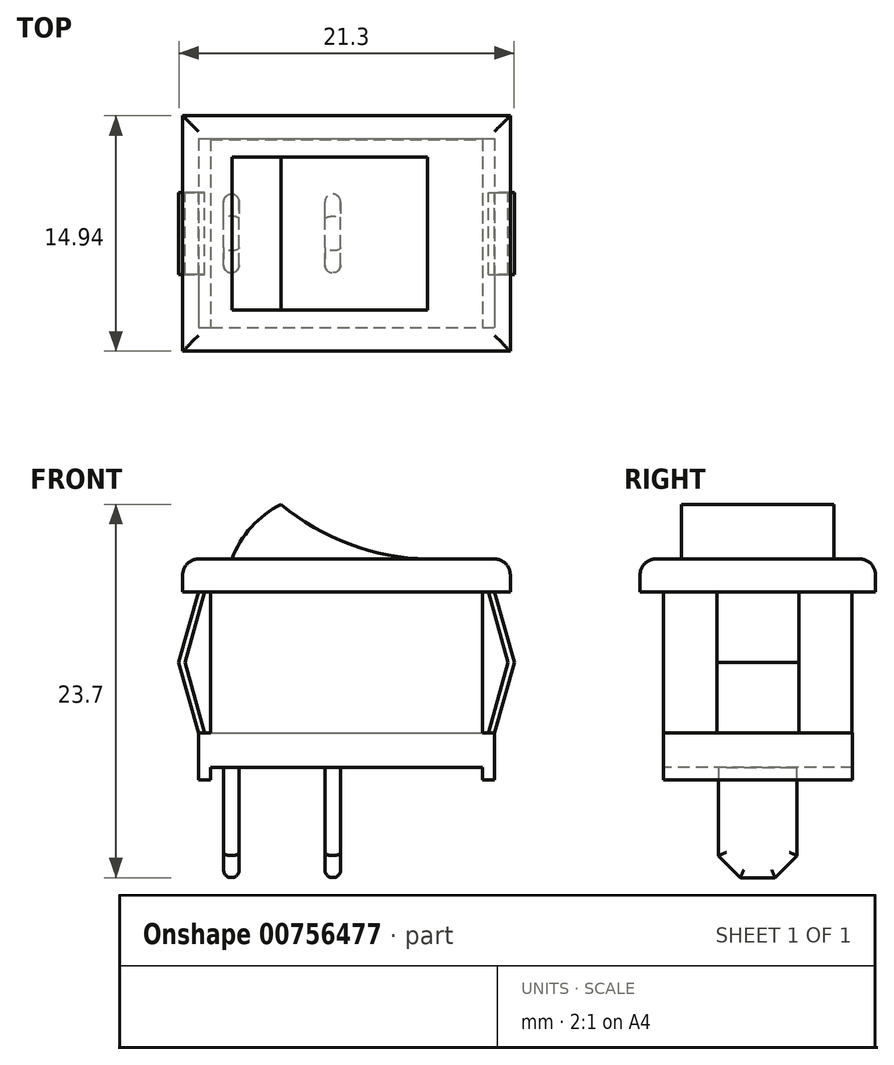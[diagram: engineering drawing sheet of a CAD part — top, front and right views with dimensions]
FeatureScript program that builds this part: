
annotation { "Feature Type Name" : "Feature", "Feature Type Description" : "" }
export const myFeature = defineFeature(function(context is Context, id is Id, definition is map)
    precondition{}
    {
        {
            var Q0;
            Q0=qCreatedBy(makeId("Front.planeOp"),FACE);
            var sketch = newSketch(context, id + "F0", { "sketchPlane" : qUnion([Q0])});
            skLineSegment(sketch, "E0.bottom", {"start": v(-8.62, -5.47) * mm, "end": v(8.62, -5.47) * mm});
            skLineSegment(sketch, "E0.top", {"start": v(-8.62, 5.47) * mm, "end": v(8.62, 5.47) * mm});
            skLineSegment(sketch, "E0.left", {"start": v(-8.62, -5.48) * mm, "end": v(-8.62, 5.47) * mm});
            skLineSegment(sketch, "E0.right", {"start": v(8.62, -5.48) * mm, "end": v(8.62, 5.47) * mm});
            skPoint(sketch, "E0.middle", {"position": v(0, 0) * mm});
            skSolve(sketch);
        }
        {
            var Q0;
            Q0=makeQuery(id+"F0.imprint","IMPRINT",FACE,{"disambiguationData":[TD([[makeQuery(id+"F0.imprint","IMPRINT",EDGE,{"derivedFrom":sQuery(id+"F0.wireOp",EDGE,"E0.bottom")}),1.0]])]});
            extrude(context, id + "F1", {"entities" : qUnion([Q0]), "depth" : 11.95 * mm, "offsetDistance" : 25 * mm, "symmetric" : true});
        }
        {
            var Q0;
            Q0=makeQuery(id+"F1.opExtrude","CAP_FACE",FACE,{"disambiguationData":[OSD([sQuery(id+"F0.wireOp",EDGE,"E0.bottom"),sQuery(id+"F0.wireOp",EDGE,"E0.top"),sQuery(id+"F0.wireOp",EDGE,"E0.left"),sQuery(id+"F0.wireOp",EDGE,"E0.right")])],"isStart":false});
            var sketch = newSketch(context, id + "F2", { "sketchPlane" : qUnion([Q0])});
            skLineSegment(sketch, "E1.0", {"start": v(8.62, -5.48) * mm, "end": v(8.62, 5.47) * mm});
            skLineSegment(sketch, "E1.1", {"start": v(-8.62, -5.47) * mm, "end": v(8.62, -5.47) * mm});
            skLineSegment(sketch, "E1.2", {"start": v(-8.62, -5.48) * mm, "end": v(-8.62, 5.47) * mm});
            skLineSegment(sketch, "E2", {"start": v(0, -3.47) * mm, "end": v(-9.4, -3.48) * mm});
            skLineSegment(sketch, "E3", {"start": v(-9.4, -3.48) * mm, "end": v(-9.4, -6.47) * mm});
            skLineSegment(sketch, "E4", {"start": v(-9.4, -6.47) * mm, "end": v(0, -6.47) * mm});
            skLineSegment(sketch, "E5", {"start": v(0, 0) * mm, "end": v(0, -5.47) * mm, "construction": true});
            skLineSegment(sketch, "E6.MirrorCS", {"start": v(0, -3.47) * mm, "end": v(9.4, -3.48) * mm});
            skLineSegment(sketch, "E7.MirrorCS", {"start": v(9.4, -3.48) * mm, "end": v(9.4, -6.47) * mm});
            skLineSegment(sketch, "E8.MirrorCS", {"start": v(9.4, -6.47) * mm, "end": v(0, -6.47) * mm});
            skSolve(sketch);
        }
        {
            var Q0;
            {var subQ1=sQuery(id+"F2.wireOp",EDGE,"E1.1");Q0=makeQuery(id+"F2.imprint","IMPRINT",FACE,{"disambiguationData":[TD([[makeQuery(id+"F2.imprint","IMPRINT",EDGE,{"derivedFrom":subQ1}),1.0]])]});}
            var Q1;
            {var subQ4=sQuery(id+"F2.wireOp",EDGE,"E1.1");Q1=makeQuery(id+"F2.imprint","IMPRINT",FACE,{"disambiguationData":[TD([[makeQuery(id+"F2.imprint","IMPRINT",EDGE,{"derivedFrom":subQ4}),-1.0]])]});}
            extrude(context, id + "F3", {"entities" : qUnion([Q0, Q1]), "operationType" : NewBodyOperationType.ADD, "oppositeDirection" : true, "depth" : 12 * mm, "offsetDistance" : 25 * mm});
        }
        {
            var Q0;
            Q0=makeQuery(id+"F3.boolean.opBoolean","MERGE",FACE,{"derivedFrom":[makeQuery(id+"F1.opExtrude","CAP_FACE",FACE,{"disambiguationData":[OSD([sQuery(id+"F0.wireOp",EDGE,"E0.bottom"),sQuery(id+"F0.wireOp",EDGE,"E0.top"),sQuery(id+"F0.wireOp",EDGE,"E0.left"),sQuery(id+"F0.wireOp",EDGE,"E0.right")])],"isStart":false}),makeQuery(id+"F3.opExtrude","CAP_FACE",FACE,{"disambiguationData":[OSD([sQuery(id+"F2.wireOp",EDGE,"E2"),sQuery(id+"F2.wireOp",EDGE,"E3"),sQuery(id+"F2.wireOp",EDGE,"E4"),sQuery(id+"F2.wireOp",EDGE,"E6.MirrorCS"),sQuery(id+"F2.wireOp",EDGE,"E7.MirrorCS"),sQuery(id+"F2.wireOp",EDGE,"E8.MirrorCS")])],"isStart":true})]});
            var sketch = newSketch(context, id + "F4", { "sketchPlane" : qUnion([Q0])});
            skLineSegment(sketch, "E9.0", {"start": v(-9.4, -6.47) * mm, "end": v(9.4, -6.47) * mm});
            skLineSegment(sketch, "E9.1", {"start": v(8.62, -3.47) * mm, "end": v(8.62, 5.47) * mm});
            skLineSegment(sketch, "E9.2", {"start": v(-8.62, -3.47) * mm, "end": v(-8.62, 5.47) * mm});
            skLineSegment(sketch, "E10.bottom", {"start": v(-8.62, -5.67) * mm, "end": v(8.62, -5.67) * mm});
            skLineSegment(sketch, "E10.top", {"start": v(-8.62, -6.47) * mm, "end": v(8.62, -6.47) * mm});
            skLineSegment(sketch, "E10.left", {"start": v(-8.62, -5.67) * mm, "end": v(-8.62, -6.47) * mm});
            skLineSegment(sketch, "E10.right", {"start": v(8.62, -5.67) * mm, "end": v(8.62, -6.47) * mm});
            skSolve(sketch);
        }
        {
            var Q0;
            Q0=makeQuery(id+"F4.imprint","IMPRINT",FACE,{"disambiguationData":[TD([[makeQuery(id+"F4.imprint","IMPRINT",EDGE,{"derivedFrom":sQuery(id+"F4.wireOp",EDGE,"E10.bottom")}),-1.0]])]});
            extrude(context, id + "F5", {"entities" : qUnion([Q0]), "operationType" : NewBodyOperationType.REMOVE, "endBound" : BoundingType.THROUGH_ALL, "oppositeDirection" : true, "depth" : 25 * mm, "offsetDistance" : 25 * mm});
        }
        {
            var Q0;
            Q0=qCreatedBy(makeId("Front.planeOp"),FACE);
            var sketch = newSketch(context, id + "F6", { "sketchPlane" : qUnion([Q0])});
            skLineSegment(sketch, "E11.0", {"start": v(8.62, -3.47) * mm, "end": v(8.62, 5.47) * mm});
            skLineSegment(sketch, "E11.1", {"start": v(-8.62, -3.47) * mm, "end": v(-8.62, 5.47) * mm});
            skLineSegment(sketch, "E12", {"start": v(0, 5.48) * mm, "end": v(0, -5.67) * mm, "construction": true});
            skLineSegment(sketch, "E13", {"start": v(-8.62, 1) * mm, "end": v(8.62, 1) * mm, "construction": true});
            skLineSegment(sketch, "E14", {"start": v(-9.4, -3.47) * mm, "end": v(-10.65, 1) * mm});
            skLineSegment(sketch, "E15", {"start": v(-10.65, 1) * mm, "end": v(-9.4, 5.48) * mm});
            skLineSegment(sketch, "E16", {"start": v(-9.01, -3.47) * mm, "end": v(-10.27, 1) * mm});
            skLineSegment(sketch, "E17", {"start": v(-10.27, 1) * mm, "end": v(-9.01, 5.48) * mm});
            skLineSegment(sketch, "E18", {"start": v(-9.4, 5.47) * mm, "end": v(-9.01, 5.47) * mm});
            skLineSegment(sketch, "E19.MirrorCS", {"start": v(9.01, -3.47) * mm, "end": v(10.27, 1) * mm});
            skLineSegment(sketch, "E20.MirrorCS", {"start": v(9.4, -3.47) * mm, "end": v(10.65, 1) * mm});
            skLineSegment(sketch, "E21.MirrorCS", {"start": v(10.27, 1) * mm, "end": v(9.01, 5.48) * mm});
            skLineSegment(sketch, "E22.MirrorCS", {"start": v(10.65, 1) * mm, "end": v(9.4, 5.48) * mm});
            skLineSegment(sketch, "E23.MirrorCS", {"start": v(9.4, 5.47) * mm, "end": v(9.01, 5.47) * mm});
            skLineSegment(sketch, "E24.0", {"start": v(-9.4, -3.47) * mm, "end": v(-8.62, -3.47) * mm});
            skLineSegment(sketch, "E25.0", {"start": v(8.62, -3.48) * mm, "end": v(9.4, -3.48) * mm});
            skSolve(sketch);
        }
        {
            var Q0;
            {var subQ1=sQuery(id+"F6.wireOp",EDGE,"E14");Q0=makeQuery(id+"F6.imprint","IMPRINT",FACE,{"disambiguationData":[TD([[makeQuery(id+"F6.imprint","IMPRINT",EDGE,{"derivedFrom":subQ1}),-1.0]])]});}
            var Q1;
            {var subQ1=sQuery(id+"F6.wireOp",EDGE,"E19.MirrorCS");Q1=makeQuery(id+"F6.imprint","IMPRINT",FACE,{"disambiguationData":[TD([[makeQuery(id+"F6.imprint","IMPRINT",EDGE,{"derivedFrom":subQ1}),-1.0]])]});}
            extrude(context, id + "F7", {"entities" : qUnion([Q0, Q1]), "operationType" : NewBodyOperationType.ADD, "depth" : 5.2 * mm, "offsetDistance" : 25 * mm, "symmetric" : true});
        }
        {
            var Q0;
            Q0=qCreatedBy(makeId("Front.planeOp"),FACE);
            var sketch = newSketch(context, id + "F8", { "sketchPlane" : qUnion([Q0])});
            skLineSegment(sketch, "E26.0", {"start": v(-8.62, 5.47) * mm, "end": v(8.62, 5.47) * mm});
            skLineSegment(sketch, "E27", {"start": v(-10.4, 5.47) * mm, "end": v(10.4, 5.47) * mm});
            skPoint(sketch, "E28", {"position": v(0, 5.47) * mm});
            skLineSegment(sketch, "E29", {"start": v(10.4, 5.47) * mm, "end": v(10.4, 7.58) * mm});
            skLineSegment(sketch, "E30", {"start": v(10.4, 7.58) * mm, "end": v(-10.4, 7.58) * mm});
            skLineSegment(sketch, "E31", {"start": v(-10.4, 7.58) * mm, "end": v(-10.4, 5.47) * mm});
            skSolve(sketch);
        }
        {
            var Q0;
            {var subQ2=sQuery(id+"F8.wireOp",EDGE,"E29");Q0=makeQuery(id+"F8.imprint","IMPRINT",FACE,{"disambiguationData":[TD([[makeQuery(id+"F8.imprint","IMPRINT",EDGE,{"derivedFrom":subQ2}),1.0]])]});}
            extrude(context, id + "F9", {"entities" : qUnion([Q0]), "operationType" : NewBodyOperationType.ADD, "depth" : 14.95 * mm, "offsetDistance" : 25 * mm, "symmetric" : true});
        }
        {
            var Q0;
            Q0=makeQuery(id+"F5.boolean.opBoolean","COPY",FACE,{"derivedFrom":makeQuery(id+"F5.opExtrude","SWEPT_FACE",FACE,{"disambiguationData":[OSD([sQuery(id+"F4.wireOp",EDGE,"E10.bottom")])]})});
            var sketch = newSketch(context, id + "F10", { "sketchPlane" : qUnion([Q0])});
            skLineSegment(sketch, "E32.bottom", {"start": v(-0.38, 2.5) * mm, "end": v(-1.38, 2.5) * mm});
            skLineSegment(sketch, "E32.top", {"start": v(-0.37, -2.5) * mm, "end": v(-1.37, -2.5) * mm});
            skLineSegment(sketch, "E32.left", {"start": v(-0.38, 2.5) * mm, "end": v(-0.37, -2.5) * mm});
            skLineSegment(sketch, "E32.right", {"start": v(-1.38, 2.5) * mm, "end": v(-1.37, -2.5) * mm});
            skPoint(sketch, "E33", {"position": v(-0.38, 0) * mm});
            skLineSegment(sketch, "E34", {"start": v(0, 0) * mm, "end": v(-8.62, 0) * mm, "construction": true});
            skLineSegment(sketch, "E35.bottom", {"start": v(-6.81, 2.5) * mm, "end": v(-7.81, 2.5) * mm});
            skLineSegment(sketch, "E35.top", {"start": v(-6.81, -2.5) * mm, "end": v(-7.81, -2.5) * mm});
            skLineSegment(sketch, "E35.left", {"start": v(-6.81, 2.5) * mm, "end": v(-6.81, -2.5) * mm});
            skLineSegment(sketch, "E35.right", {"start": v(-7.81, 2.5) * mm, "end": v(-7.81, -2.5) * mm});
            skPoint(sketch, "E36", {"position": v(-6.81, 0) * mm});
            skSolve(sketch);
        }
        {
            var Q0;
            Q0=makeQuery(id+"F10.imprint","IMPRINT",FACE,{"disambiguationData":[TD([[makeQuery(id+"F10.imprint","IMPRINT",EDGE,{"derivedFrom":sQuery(id+"F10.wireOp",EDGE,"E35.bottom")}),1.0]])]});
            var Q1;
            Q1=makeQuery(id+"F10.imprint","IMPRINT",FACE,{"disambiguationData":[TD([[makeQuery(id+"F10.imprint","IMPRINT",EDGE,{"derivedFrom":sQuery(id+"F10.wireOp",EDGE,"E32.bottom")}),1.0]])]});
            extrude(context, id + "F11", {"entities" : qUnion([Q0, Q1]), "operationType" : NewBodyOperationType.ADD, "depth" : 7 * mm, "offsetDistance" : 25 * mm});
        }
        {
            var Q0;
            Q0=makeQuery(id+"F11.opExtrude","CAP_EDGE",EDGE,{"disambiguationData":[OSD([sQuery(id+"F10.wireOp",EDGE,"E35.bottom")])],"isStart":false});
            var Q1;
            Q1=makeQuery(id+"F11.opExtrude","CAP_EDGE",EDGE,{"disambiguationData":[OSD([sQuery(id+"F10.wireOp",EDGE,"E35.top")])],"isStart":false});
            var Q2;
            Q2=makeQuery(id+"F11.opExtrude","CAP_EDGE",EDGE,{"disambiguationData":[OSD([sQuery(id+"F10.wireOp",EDGE,"E32.bottom")])],"isStart":false});
            var Q3;
            Q3=makeQuery(id+"F11.opExtrude","CAP_EDGE",EDGE,{"disambiguationData":[OSD([sQuery(id+"F10.wireOp",EDGE,"E32.top")])],"isStart":false});
            chamfer(context, id + "F12", {"entities" : qUnion([Q0, Q1, Q2, Q3]), "width" : 1.4 * mm, "tangentPropagation" : true});
        }
        {
            var Q0;
            Q0=makeQuery(id+"F11.opExtrude","SWEPT_EDGE",EDGE,{"disambiguationData":[OSD([sQuery(id+"F10.wireOp",EDGE,"E35.bottom"),sQuery(id+"F10.wireOp",EDGE,"E35.left")])]});
            var Q1;
            Q1=makeQuery(id+"F11.opExtrude","SWEPT_EDGE",EDGE,{"disambiguationData":[OSD([sQuery(id+"F10.wireOp",EDGE,"E35.bottom"),sQuery(id+"F10.wireOp",EDGE,"E35.right")])]});
            var Q2;
            Q2=makeQuery(id+"F12.opChamfer","BLEND_EDGE",EDGE,{"blendedFrom":[makeQuery(id+"F11.opExtrude","CAP_EDGE",EDGE,{"disambiguationData":[OSD([sQuery(id+"F10.wireOp",EDGE,"E35.bottom")])],"isStart":false}),makeQuery(id+"F11.opExtrude","SWEPT_FACE",FACE,{"disambiguationData":[OSD([sQuery(id+"F10.wireOp",EDGE,"E35.left")])]})],"blendedInto":[makeQuery(id+"F11.opExtrude","SWEPT_FACE",FACE,{"disambiguationData":[OSD([sQuery(id+"F10.wireOp",EDGE,"E35.left")])]})]});
            var Q3;
            Q3=makeQuery(id+"F12.opChamfer","BLEND_EDGE",EDGE,{"blendedFrom":[makeQuery(id+"F11.opExtrude","CAP_EDGE",EDGE,{"disambiguationData":[OSD([sQuery(id+"F10.wireOp",EDGE,"E35.bottom")])],"isStart":false}),makeQuery(id+"F11.opExtrude","SWEPT_FACE",FACE,{"disambiguationData":[OSD([sQuery(id+"F10.wireOp",EDGE,"E35.right")])]})],"blendedInto":[makeQuery(id+"F11.opExtrude","SWEPT_FACE",FACE,{"disambiguationData":[OSD([sQuery(id+"F10.wireOp",EDGE,"E35.right")])]})]});
            var Q4;
            Q4=makeQuery(id+"F11.opExtrude","CAP_EDGE",EDGE,{"disambiguationData":[OSD([sQuery(id+"F10.wireOp",EDGE,"E35.left")])],"isStart":false});
            var Q5;
            Q5=makeQuery(id+"F11.opExtrude","CAP_EDGE",EDGE,{"disambiguationData":[OSD([sQuery(id+"F10.wireOp",EDGE,"E35.right")])],"isStart":false});
            var Q6;
            Q6=makeQuery(id+"F12.opChamfer","BLEND_EDGE",EDGE,{"blendedFrom":[makeQuery(id+"F11.opExtrude","CAP_EDGE",EDGE,{"disambiguationData":[OSD([sQuery(id+"F10.wireOp",EDGE,"E35.top")])],"isStart":false}),makeQuery(id+"F11.opExtrude","SWEPT_FACE",FACE,{"disambiguationData":[OSD([sQuery(id+"F10.wireOp",EDGE,"E35.left")])]})],"blendedInto":[makeQuery(id+"F11.opExtrude","SWEPT_FACE",FACE,{"disambiguationData":[OSD([sQuery(id+"F10.wireOp",EDGE,"E35.left")])]})]});
            var Q7;
            Q7=makeQuery(id+"F12.opChamfer","BLEND_EDGE",EDGE,{"blendedFrom":[makeQuery(id+"F11.opExtrude","CAP_EDGE",EDGE,{"disambiguationData":[OSD([sQuery(id+"F10.wireOp",EDGE,"E35.top")])],"isStart":false}),makeQuery(id+"F11.opExtrude","SWEPT_FACE",FACE,{"disambiguationData":[OSD([sQuery(id+"F10.wireOp",EDGE,"E35.right")])]})],"blendedInto":[makeQuery(id+"F11.opExtrude","SWEPT_FACE",FACE,{"disambiguationData":[OSD([sQuery(id+"F10.wireOp",EDGE,"E35.right")])]})]});
            var Q8;
            Q8=makeQuery(id+"F11.opExtrude","SWEPT_EDGE",EDGE,{"disambiguationData":[OSD([sQuery(id+"F10.wireOp",EDGE,"E35.top"),sQuery(id+"F10.wireOp",EDGE,"E35.left")])]});
            var Q9;
            Q9=makeQuery(id+"F11.opExtrude","SWEPT_EDGE",EDGE,{"disambiguationData":[OSD([sQuery(id+"F10.wireOp",EDGE,"E35.top"),sQuery(id+"F10.wireOp",EDGE,"E35.right")])]});
            var Q10;
            Q10=makeQuery(id+"F11.opExtrude","SWEPT_EDGE",EDGE,{"disambiguationData":[OSD([sQuery(id+"F10.wireOp",EDGE,"E32.top"),sQuery(id+"F10.wireOp",EDGE,"E32.left")])]});
            var Q11;
            Q11=makeQuery(id+"F11.opExtrude","SWEPT_EDGE",EDGE,{"disambiguationData":[OSD([sQuery(id+"F10.wireOp",EDGE,"E32.top"),sQuery(id+"F10.wireOp",EDGE,"E32.right")])]});
            var Q12;
            Q12=makeQuery(id+"F12.opChamfer","BLEND_EDGE",EDGE,{"blendedFrom":[makeQuery(id+"F11.opExtrude","CAP_EDGE",EDGE,{"disambiguationData":[OSD([sQuery(id+"F10.wireOp",EDGE,"E32.top")])],"isStart":false}),makeQuery(id+"F11.opExtrude","SWEPT_FACE",FACE,{"disambiguationData":[OSD([sQuery(id+"F10.wireOp",EDGE,"E32.left")])]})],"blendedInto":[makeQuery(id+"F11.opExtrude","SWEPT_FACE",FACE,{"disambiguationData":[OSD([sQuery(id+"F10.wireOp",EDGE,"E32.left")])]})]});
            var Q13;
            Q13=makeQuery(id+"F12.opChamfer","BLEND_EDGE",EDGE,{"blendedFrom":[makeQuery(id+"F11.opExtrude","CAP_EDGE",EDGE,{"disambiguationData":[OSD([sQuery(id+"F10.wireOp",EDGE,"E32.top")])],"isStart":false}),makeQuery(id+"F11.opExtrude","SWEPT_FACE",FACE,{"disambiguationData":[OSD([sQuery(id+"F10.wireOp",EDGE,"E32.right")])]})],"blendedInto":[makeQuery(id+"F11.opExtrude","SWEPT_FACE",FACE,{"disambiguationData":[OSD([sQuery(id+"F10.wireOp",EDGE,"E32.right")])]})]});
            var Q14;
            Q14=makeQuery(id+"F11.opExtrude","CAP_EDGE",EDGE,{"disambiguationData":[OSD([sQuery(id+"F10.wireOp",EDGE,"E32.left")])],"isStart":false});
            var Q15;
            Q15=makeQuery(id+"F11.opExtrude","CAP_EDGE",EDGE,{"disambiguationData":[OSD([sQuery(id+"F10.wireOp",EDGE,"E32.right")])],"isStart":false});
            var Q16;
            Q16=makeQuery(id+"F12.opChamfer","BLEND_EDGE",EDGE,{"blendedFrom":[makeQuery(id+"F11.opExtrude","CAP_EDGE",EDGE,{"disambiguationData":[OSD([sQuery(id+"F10.wireOp",EDGE,"E32.bottom")])],"isStart":false}),makeQuery(id+"F11.opExtrude","SWEPT_FACE",FACE,{"disambiguationData":[OSD([sQuery(id+"F10.wireOp",EDGE,"E32.left")])]})],"blendedInto":[makeQuery(id+"F11.opExtrude","SWEPT_FACE",FACE,{"disambiguationData":[OSD([sQuery(id+"F10.wireOp",EDGE,"E32.left")])]})]});
            var Q17;
            Q17=makeQuery(id+"F12.opChamfer","BLEND_EDGE",EDGE,{"blendedFrom":[makeQuery(id+"F11.opExtrude","CAP_EDGE",EDGE,{"disambiguationData":[OSD([sQuery(id+"F10.wireOp",EDGE,"E32.bottom")])],"isStart":false}),makeQuery(id+"F11.opExtrude","SWEPT_FACE",FACE,{"disambiguationData":[OSD([sQuery(id+"F10.wireOp",EDGE,"E32.right")])]})],"blendedInto":[makeQuery(id+"F11.opExtrude","SWEPT_FACE",FACE,{"disambiguationData":[OSD([sQuery(id+"F10.wireOp",EDGE,"E32.right")])]})]});
            var Q18;
            Q18=makeQuery(id+"F11.opExtrude","SWEPT_EDGE",EDGE,{"disambiguationData":[OSD([sQuery(id+"F10.wireOp",EDGE,"E32.bottom"),sQuery(id+"F10.wireOp",EDGE,"E32.left")])]});
            var Q19;
            Q19=makeQuery(id+"F11.opExtrude","SWEPT_EDGE",EDGE,{"disambiguationData":[OSD([sQuery(id+"F10.wireOp",EDGE,"E32.bottom"),sQuery(id+"F10.wireOp",EDGE,"E32.right")])]});
            fillet(context, id + "F13", {"entities" : qUnion([Q0, Q1, Q2, Q3, Q4, Q5, Q6, Q7, Q8, Q9, Q10, Q11, Q12, Q13, Q14, Q15, Q16, Q17, Q18, Q19]), "radius" : .5 * mm, "tangentPropagation" : true, "allowEdgeOverflow" : false});
        }
        {
            var Q0;
            Q0=makeQuery(id+"F9.opExtrude","CAP_EDGE",EDGE,{"disambiguationData":[OSD([sQuery(id+"F8.wireOp",EDGE,"E30")])],"isStart":false});
            var Q1;
            Q1=makeQuery(id+"F9.opExtrude","SWEPT_EDGE",EDGE,{"disambiguationData":[OSD([sQuery(id+"F8.wireOp",EDGE,"E29"),sQuery(id+"F8.wireOp",EDGE,"E30")])]});
            var Q2;
            Q2=makeQuery(id+"F9.opExtrude","CAP_EDGE",EDGE,{"disambiguationData":[OSD([sQuery(id+"F8.wireOp",EDGE,"E30")])],"isStart":true});
            var Q3;
            Q3=makeQuery(id+"F9.opExtrude","SWEPT_EDGE",EDGE,{"disambiguationData":[OSD([sQuery(id+"F8.wireOp",EDGE,"E30"),sQuery(id+"F8.wireOp",EDGE,"E31")])]});
            fillet(context, id + "F14", {"entities" : qUnion([Q0, Q1, Q2, Q3]), "radius" : 1 * mm, "tangentPropagation" : true, "allowEdgeOverflow" : false});
        }
        {
            var Q0;
            Q0=qCreatedBy(makeId("Front.planeOp"),FACE);
            var sketch = newSketch(context, id + "F15", { "sketchPlane" : qUnion([Q0])});
            skLineSegment(sketch, "E37.0", {"start": v(-9.4, 7.58) * mm, "end": v(9.4, 7.58) * mm});
            skArc(sketch, "E38", {"start": v(-4.16, 11.03) * mm, "mid": v(0.45, 8.42) * mm, "end": v(5.68, 7.58) * mm});
            skArc(sketch, "E39", {"start": v(-4.16, 11.03) * mm, "mid": v(-6.05, 9.6) * mm, "end": v(-7.27, 7.58) * mm});
            skSolve(sketch);
        }
        {
            var Q0;
            {var subQ0=sQuery(id+"F15.wireOp",EDGE,"E39");Q0=makeQuery(id+"F15.imprint","IMPRINT",FACE,{"disambiguationData":[TD([[makeQuery(id+"F15.imprint","IMPRINT",EDGE,{"derivedFrom":subQ0}),1.0]])]});}
            extrude(context, id + "F16", {"entities" : qUnion([Q0]), "operationType" : NewBodyOperationType.ADD, "depth" : 9.7 * mm, "offsetDistance" : 25 * mm, "symmetric" : true});
        }
    });
